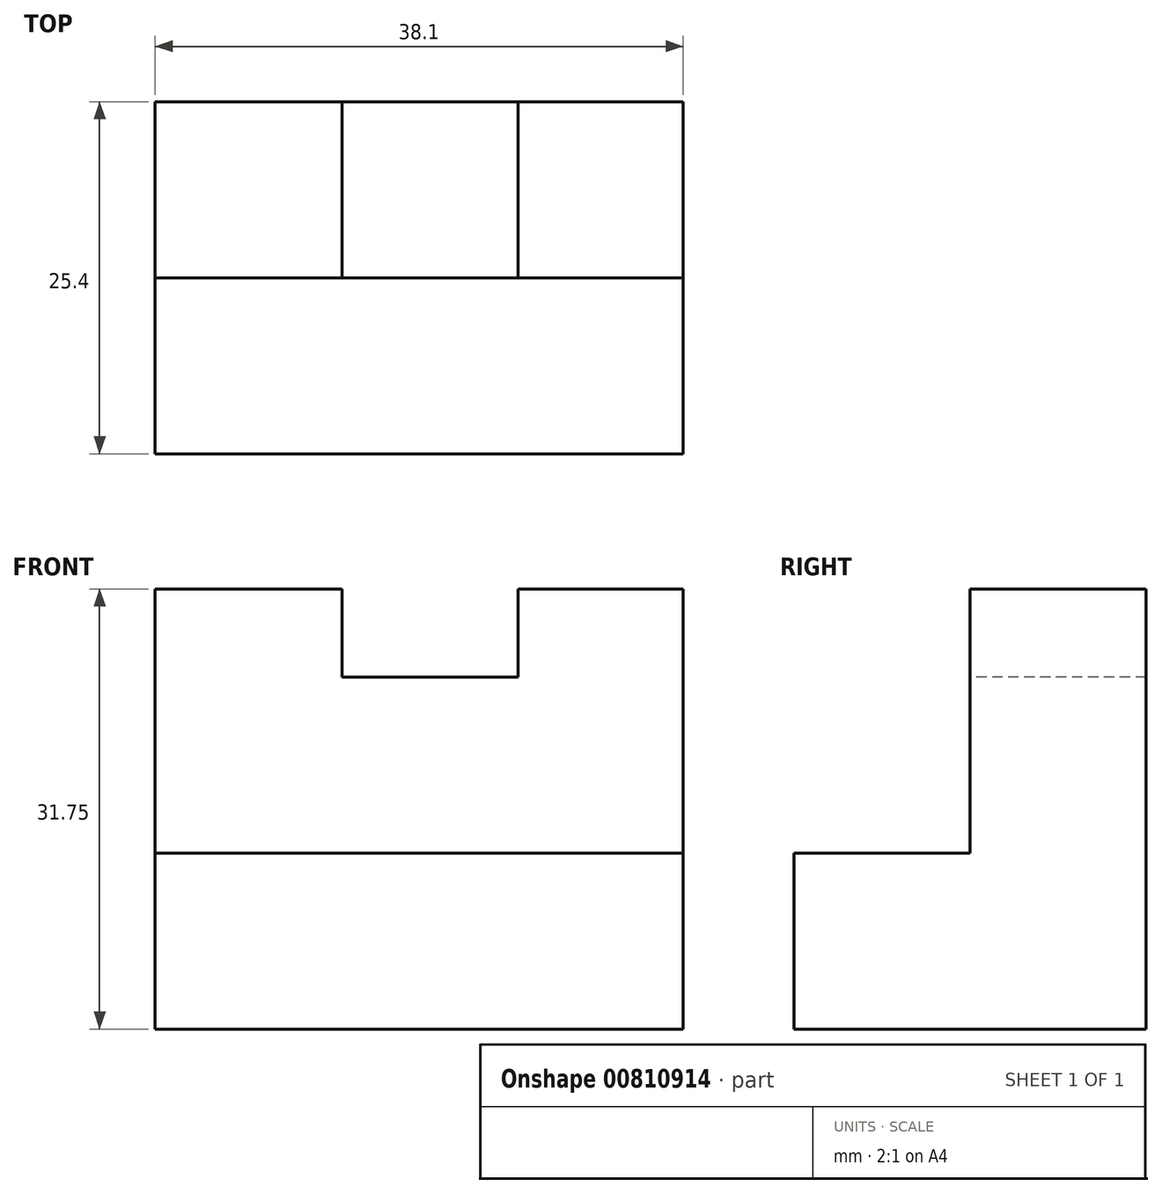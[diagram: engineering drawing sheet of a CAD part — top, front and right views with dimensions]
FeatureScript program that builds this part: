
annotation { "Feature Type Name" : "Feature", "Feature Type Description" : "" }
export const myFeature = defineFeature(function(context is Context, id is Id, definition is map)
    precondition{}
    {
        {
            var Q0;
            Q0=qCreatedBy(makeId("Top.planeOp"),FACE);
            var sketch = newSketch(context, id + "F0", { "sketchPlane" : qUnion([Q0])});
            skLineSegment(sketch, "E0.bottom", {"start": v(0, 0) * mm, "end": v(38.1, 0) * mm});
            skLineSegment(sketch, "E0.top", {"start": v(0, 25.4) * mm, "end": v(38.1, 25.4) * mm});
            skLineSegment(sketch, "E0.left", {"start": v(0, 0) * mm, "end": v(0, 25.4) * mm});
            skLineSegment(sketch, "E0.right", {"start": v(38.1, 0) * mm, "end": v(38.1, 25.4) * mm});
            skSolve(sketch);
        }
        {
            var Q0;
            Q0=makeQuery(id+"F0.imprint","IMPRINT",FACE,{"disambiguationData":[TD([[makeQuery(id+"F0.imprint","IMPRINT",EDGE,{"derivedFrom":sQuery(id+"F0.wireOp",EDGE,"E0.bottom")}),1.0]])]});
            extrude(context, id + "F1", {"entities" : qUnion([Q0]), "depth" : 31.75 * mm, "offsetDistance" : 25.4 * mm});
        }
        {
            var Q0;
            Q0=makeQuery(id+"F1.opExtrude","SWEPT_FACE",FACE,{"disambiguationData":[OSD([sQuery(id+"F0.wireOp",EDGE,"E0.right")])]});
            var sketch = newSketch(context, id + "F2", { "sketchPlane" : qUnion([Q0])});
            skLineSegment(sketch, "E1", {"start": v(0, 0) * mm, "end": v(0, 12.7) * mm});
            skLineSegment(sketch, "E2", {"start": v(0, 12.7) * mm, "end": v(12.7, 12.7) * mm});
            skPoint(sketch, "E2.endSnap0", {"position": v(12.7, 0) * mm});
            skLineSegment(sketch, "E3", {"start": v(12.7, 12.7) * mm, "end": v(12.7, 31.75) * mm});
            skSolve(sketch);
        }
        {
            var Q0;
            {var subQ0=sQuery(id+"F2.wireOp",EDGE,"E2");Q0=makeQuery(id+"F2.imprint","IMPRINT",FACE,{"disambiguationData":[TD([[makeQuery(id+"F2.imprint","IMPRINT",EDGE,{"derivedFrom":subQ0}),1.0]])]});}
            extrude(context, id + "F3", {"entities" : qUnion([Q0]), "operationType" : NewBodyOperationType.REMOVE, "oppositeDirection" : true, "depth" : 38.1 * mm, "offsetDistance" : 25.4 * mm});
        }
        {
            var Q0;
            Q0=makeQuery(id+"F3.boolean.opBoolean","COPY",FACE,{"derivedFrom":makeQuery(id+"F3.opExtrude","SWEPT_FACE",FACE,{"disambiguationData":[OSD([sQuery(id+"F2.wireOp",EDGE,"E3")])]})});
            var sketch = newSketch(context, id + "F4", { "sketchPlane" : qUnion([Q0])});
            skLineSegment(sketch, "E4", {"start": v(13.5, 31.75) * mm, "end": v(13.5, 25.4) * mm});
            skLineSegment(sketch, "E5", {"start": v(13.5, 25.4) * mm, "end": v(26.2, 25.4) * mm});
            skLineSegment(sketch, "E6", {"start": v(26.2, 25.4) * mm, "end": v(26.2, 31.75) * mm});
            skSolve(sketch);
        }
        {
            var Q0;
            {var subQ0=sQuery(id+"F4.wireOp",EDGE,"E4");Q0=makeQuery(id+"F4.imprint","IMPRINT",FACE,{"disambiguationData":[TD([[makeQuery(id+"F4.imprint","IMPRINT",EDGE,{"derivedFrom":subQ0}),1.0]])]});}
            extrude(context, id + "F5", {"entities" : qUnion([Q0]), "operationType" : NewBodyOperationType.REMOVE, "oppositeDirection" : true, "depth" : 12.7 * mm, "offsetDistance" : 25.4 * mm});
        }
    });
